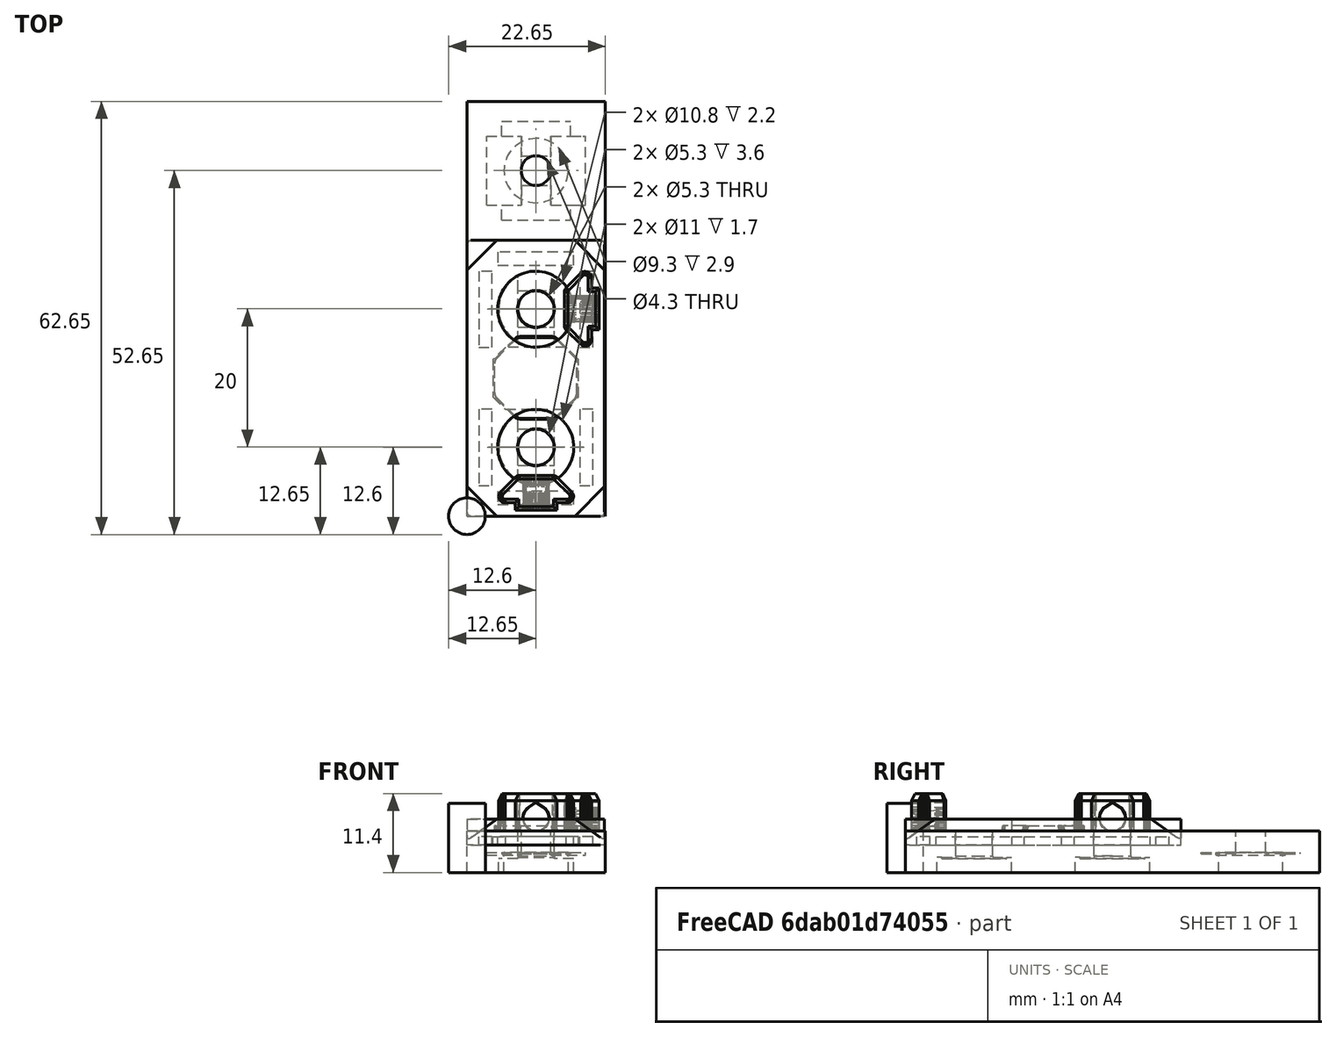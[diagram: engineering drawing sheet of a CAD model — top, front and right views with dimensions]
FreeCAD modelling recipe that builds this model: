
FCSTD DOCUMENT  (FreeCAD 0.18R14555 (Git shallow))
Label: Z-top-cap
License: All rights reserved
LicenseURL: http://en.wikipedia.org/wiki/All_rights_reserved
objects: Part::Box×9, Part::Cylinder×7, Part::Cut×6, Part::MultiFuse×4, Part::Feature×3
note: 29 computed .brp shape members not serialized (recipe doc carries the construction recipe); baked Part::Feature solids carry a one-line shape summary decoded from their .brp

FEATURE [Part::Feature] Part__Feature  label="end_cap_z_axis v13"
  Placement = pos=(0,0,4) rot=(0,0,1;0rad)
  shape: bbox 19.9 x 39.9 x 3.7 mm, 59 faces (baked)
FEATURE [Part::Feature] Incredible_Bruticus001001_solid  label="Incredible_Bruticus002 (Solid)"
  Placement = pos=(22.45,20,3) rot=(0,0,1;0rad)
  shape: bbox 19.9 x 39.9 x 8.4 mm, 640 faces (baked)
FEATURE [Part::Box] Box  label="Cube"
  AttacherType = Attacher::AttachEngine3D
  Height = 6
  Length = 20
  Width = 60
FEATURE [Part::MultiFuse] Fusion
  Shapes = -> [Incredible_Bruticus001001_solid,Box]
FEATURE [Part::Cylinder] Cylinder
  Angle = 360
  AttacherType = Attacher::AttachEngine3D
  Height = 10
  Placement = pos=(10,10,0) rot=(0,0,1;0rad)
  Radius = 2.65
FEATURE [Part::Cylinder] Cylinder001
  Angle = 360
  AttacherType = Attacher::AttachEngine3D
  Height = 10
  Placement = pos=(10,30,0) rot=(0,0,1;0rad)
  Radius = 2.65
FEATURE [Part::Cut] Cut
  Base = -> Fusion
  Tool = -> Cylinder001
FEATURE [Part::Cut] Cut001
  Base = -> Cut
  Tool = -> Cylinder
FEATURE [Part::Cylinder] Cylinder002
  Angle = 360
  AttacherType = Attacher::AttachEngine3D
  Height = 2.4
  Placement = pos=(10,10,0) rot=(0,0,1;0rad)
  Radius = 5.4
FEATURE [Part::Cylinder] Cylinder003
  Angle = 360
  AttacherType = Attacher::AttachEngine3D
  Height = 2.4
  Placement = pos=(10,30,0) rot=(0,0,1;0rad)
  Radius = 5.4
FEATURE [Part::Cut] Cut002
  Base = -> Cut001
  Tool = -> Cylinder003
FEATURE [Part::Cut] Cut003
  Base = -> Cut002
  Tool = -> Cylinder002
FEATURE [Part::Cylinder] Cylinder004
  Angle = 360
  AttacherType = Attacher::AttachEngine3D
  Height = 10
  Radius = 2.65
FEATURE [Part::Box] Box001  label="Cube001"
  AttacherType = Attacher::AttachEngine3D
  Height = 0.2
  Length = 10
  Placement = pos=(-5,-7.65,0.2) rot=(0,0,1;0rad)
  Width = 5
FEATURE [Part::Box] Box002  label="Cube002"
  AttacherType = Attacher::AttachEngine3D
  Height = 0.4
  Length = 5
  Placement = pos=(2.65,-5,0) rot=(0,0,1;0rad)
  Width = 10
FEATURE [Part::Box] Box003  label="Cube003"
  AttacherType = Attacher::AttachEngine3D
  Height = 0.4
  Length = 5
  Placement = pos=(-7.65,-5,0) rot=(0,0,1;0rad)
  Width = 10
FEATURE [Part::Box] Box004  label="Cube004"
  AttacherType = Attacher::AttachEngine3D
  Height = 0.2
  Length = 10
  Placement = pos=(-5,2.65,0.2) rot=(0,0,1;0rad)
  Width = 5
FEATURE [Part::MultiFuse] Fusion001
  Placement = pos=(10,10,2) rot=(0,0,1;0rad)
  Shapes = -> [Box001,Box004,Box003,Box002]
FEATURE [Part::Feature] Fusion001001  label="Fusion002"
  Placement = pos=(10,30,2) rot=(0,0,1;0rad)
  shape: bbox 15.3 x 15.3 x 0.4 mm, 28 faces (baked)
FEATURE [Part::MultiFuse] Fusion001002
  Shapes = -> [Fusion001001,Fusion001,Cut003]
FEATURE [Part::Box] Box005  label="Cube005"
  AttacherType = Attacher::AttachEngine3D
  Height = 0.4
  Length = 5
  Placement = pos=(-7.15,-5,0) rot=(0,0,1;0rad)
  Width = 10
FEATURE [Part::Box] Box006  label="Cube006"
  AttacherType = Attacher::AttachEngine3D
  Height = 0.4
  Length = 5
  Placement = pos=(2.15,-5,0) rot=(0,0,1;0rad)
  Width = 10
FEATURE [Part::Box] Box007  label="Cube007"
  AttacherType = Attacher::AttachEngine3D
  Height = 0.2
  Length = 10
  Placement = pos=(-5,2.15,0.2) rot=(0,0,1;0rad)
  Width = 5
FEATURE [Part::Box] Box008  label="Cube008"
  AttacherType = Attacher::AttachEngine3D
  Height = 0.2
  Length = 10
  Placement = pos=(-5,-7.15,0.2) rot=(0,0,1;0rad)
  Width = 5
FEATURE [Part::MultiFuse] Fusion001003
  Placement = pos=(10,50,2.5) rot=(0,0,1;0rad)
  Shapes = -> [Box005,Box006,Box008,Box007]
FEATURE [Part::Cylinder] Cylinder005
  Angle = 360
  AttacherType = Attacher::AttachEngine3D
  Height = 10
  Placement = pos=(10,50,0) rot=(0,0,1;0rad)
  Radius = 2.15
FEATURE [Part::Cylinder] Cylinder006
  Angle = 360
  AttacherType = Attacher::AttachEngine3D
  Height = 2.9
  Placement = pos=(10,50,0) rot=(0,0,1;0rad)
  Radius = 4.65
FEATURE [Part::Cut] Cut004
  Base = -> Fusion001002
  Tool = -> Cylinder005
FEATURE [Part::Cut] Cut005
  Base = -> Cut004
  Tool = -> Cylinder006
